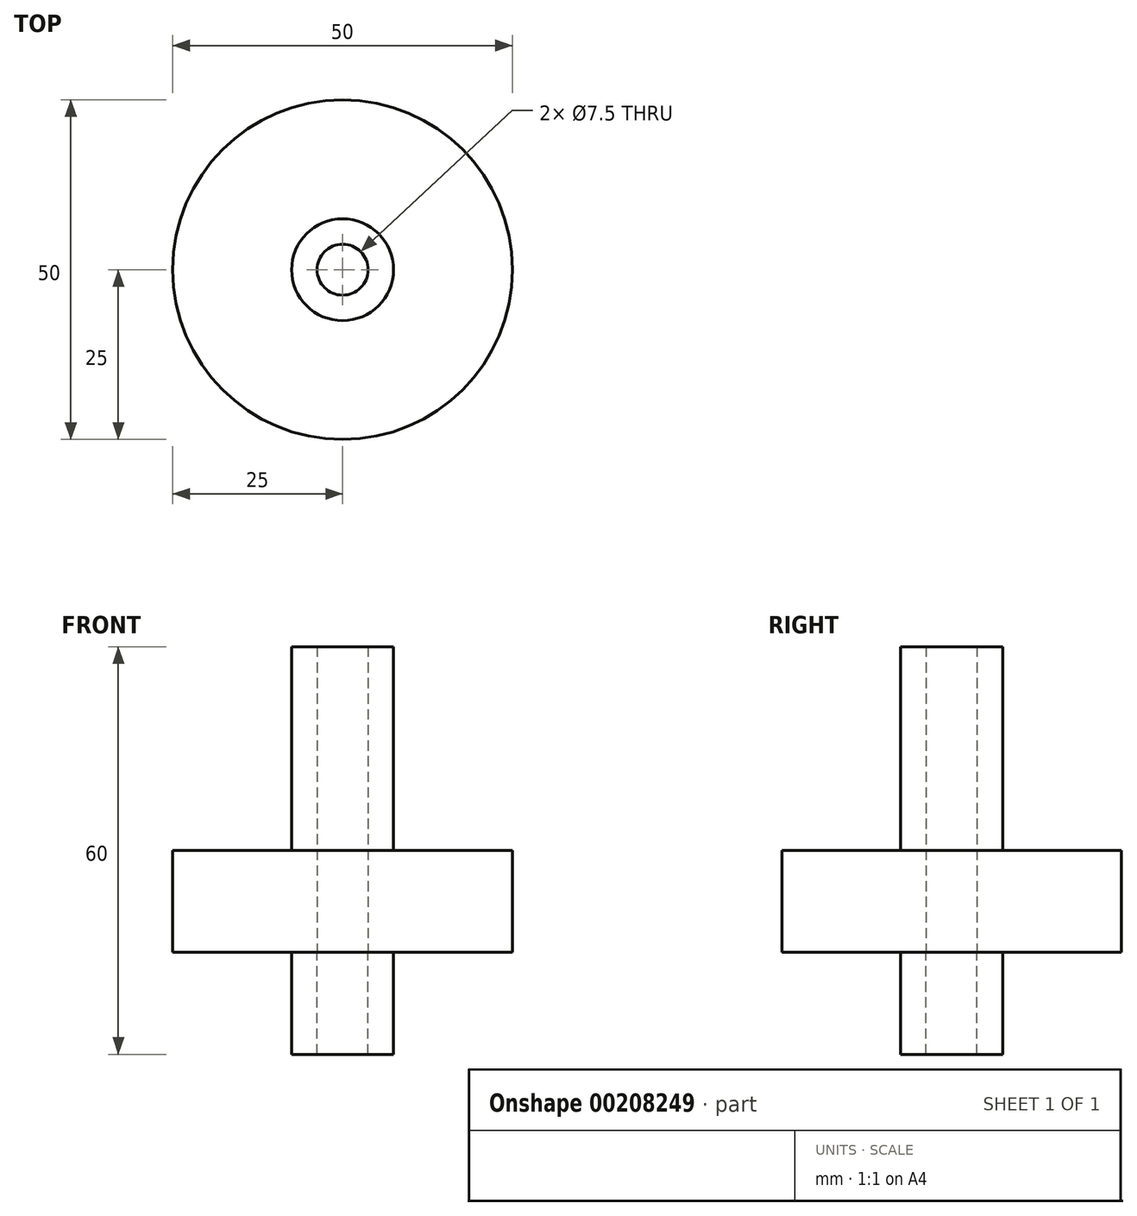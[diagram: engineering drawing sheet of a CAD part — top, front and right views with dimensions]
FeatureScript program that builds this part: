
annotation { "Feature Type Name" : "Feature", "Feature Type Description" : "" }
export const myFeature = defineFeature(function(context is Context, id is Id, definition is map)
    precondition{}
    {
        {
            var Q0;
            Q0=qCreatedBy(makeId("Top.planeOp"),FACE);
            var sketch = newSketch(context, id + "F0", { "sketchPlane" : qUnion([Q0])});
            skCircle(sketch, "E0", {"center": v(0, 0) * mm, "radius": 25 * mm});
            skCircle(sketch, "E1", {"center": v(0, 0) * mm, "radius": 7.5 * mm});
            skCircle(sketch, "E2", {"center": v(0, 0) * mm, "radius": 3.75 * mm});
            skSolve(sketch);
        }
        {
            var Q0;
            Q0=makeQuery(id+"F0.imprint","IMPRINT",FACE,{"disambiguationData":[TD([[makeQuery(id+"F0.imprint","IMPRINT",EDGE,{"derivedFrom":sQuery(id+"F0.wireOp",EDGE,"E0")}),1.0]])]});
            extrude(context, id + "F1", {"entities" : qUnion([Q0]), "depth" : 15 * mm});
        }
        {
            var Q0;
            Q0=makeQuery(id+"F0.imprint","IMPRINT",FACE,{"disambiguationData":[TD([[makeQuery(id+"F0.imprint","IMPRINT",EDGE,{"derivedFrom":sQuery(id+"F0.wireOp",EDGE,"E1")}),1.0]])]});
            var Q1;
            Q1=sQuery(id+"F0.wireOp",EDGE,"E1");
            extrude(context, id + "F2", {"entities" : qUnion([Q0]), "operationType" : NewBodyOperationType.ADD, "surfaceEntities" : qUnion([Q1]), "depth" : 45 * mm});
        }
        {
            var Q0;
            Q0=makeQuery(id+"F0.imprint","IMPRINT",FACE,{"disambiguationData":[TD([[makeQuery(id+"F0.imprint","IMPRINT",EDGE,{"derivedFrom":sQuery(id+"F0.wireOp",EDGE,"E1")}),1.0]])]});
            var Q1;
            Q1=sQuery(id+"F0.wireOp",EDGE,"E1");
            extrude(context, id + "F3", {"entities" : qUnion([Q0]), "surfaceEntities" : qUnion([Q1]), "oppositeDirection" : true, "depth" : 15 * mm});
        }
    });
